# Revit family: Lighting-Recessed- Wall-Amerlux-Passo SQ
name_source: partatom
category: Lighting Fixtures
revit_build: Autodesk Revit 2017 (Build: 20190508_0315(x64)
units: mm (PartAtom-declared; Revit-internal decimal feet)

## family parameters
Cut with Voids When Loaded = No
Host = Face
Light Source = Yes
Part Type = Normal
Room Calculation Point = No
Round Connector Dimension = Use Diameter
Shared = No

## types (7) — shared parameters
Apparent Load = 0 VA
Color Filter = 16777215
Default Elevation = 4' - 0"
Description = Recessed Wall
Dimming Lamp Color Temperature Shift = <None>
Emit from Line Length = 4' - 0"
Height = 0' - 3 1/2"
Lamp = LED
Manufacturer = Amerlux
Model = Passo SQ
Number of Poles = 1
Photometric Web File = generic
Power Factor = 1
Tilt Angle = -90.00°
URL = http://www.amerlux.com
Voltage = 0 V

## per-type parameters (varying)
| type | Length | PSCD4 | PSCD6 | PSCL4 | PSCP4 | PSCP6 | PSCS4 | PSCS6 | Width |
| PSCD4 | 0' - 3 1/2" | Yes | No | No | No | No | No | No | 0' - 3 1/2" |
| PSCL4 | 0' - 3 1/2" | No | No | Yes | No | No | No | No | 0' - 3 1/2" |
| PSCD6 | 0' - 5 15/16" | No | Yes | No | No | No | No | No | 0' - 5 15/16" |
| PSCS4 | 0' - 3 1/2" | No | No | No | No | No | Yes | No | 0' - 3 1/2" |
| PSCS6 | 0' - 6 1/4" | No | No | No | No | No | No | Yes | 0' - 6 1/4" |
| PSCP4 | 0' - 3 1/2" | No | No | No | Yes | No | No | No | 0' - 3 1/2" |
| PSCP6 | 0' - 5 15/16" | No | No | No | No | Yes | No | No | 0' - 5 15/16" |

## geometry (parser evidence)
native form markers: Sweep x16
no freeform markers — native parametric forms only
